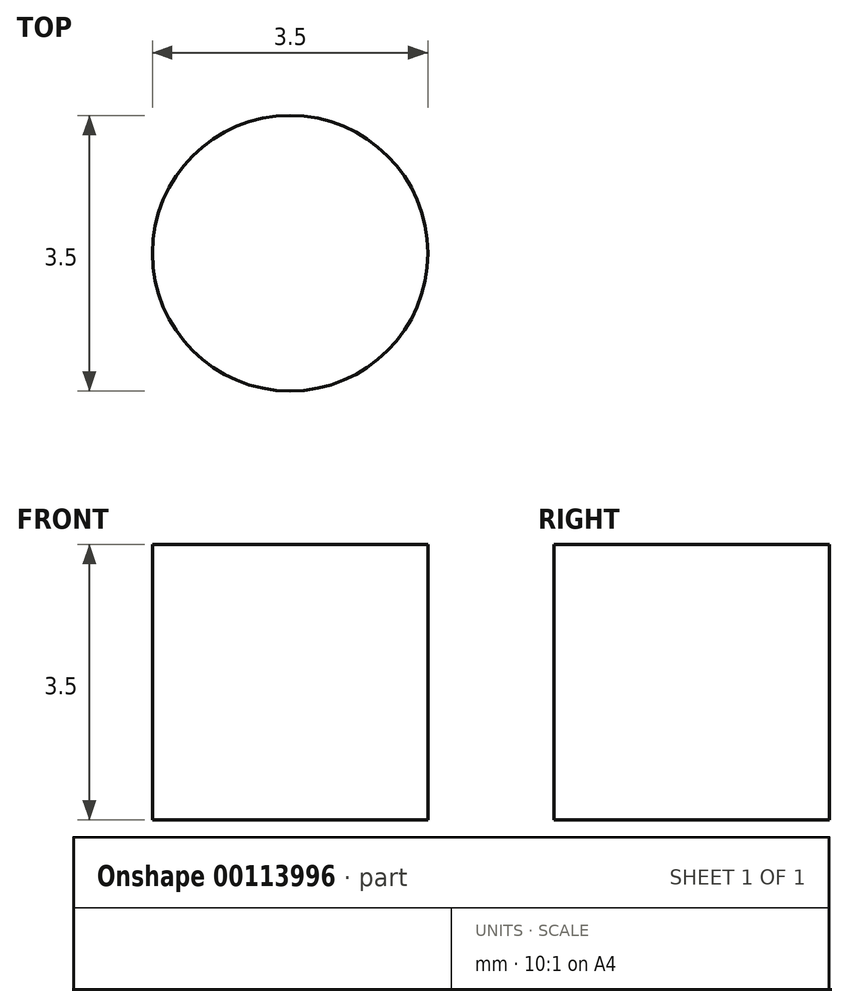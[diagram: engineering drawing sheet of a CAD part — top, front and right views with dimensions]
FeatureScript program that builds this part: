
annotation { "Feature Type Name" : "Feature", "Feature Type Description" : "" }
export const myFeature = defineFeature(function(context is Context, id is Id, definition is map)
    precondition{}
    {
        {
            var Q0;
            Q0=qCreatedBy(makeId("Right.planeOp"),FACE);
            var sketch = newSketch(context, id + "F0", { "sketchPlane" : qUnion([Q0])});
            skLineSegment(sketch, "E0.bottom", {"start": v(10, -3.07) * mm, "end": v(-10, -3.07) * mm});
            skLineSegment(sketch, "E0.top", {"start": v(10, 2.93) * mm, "end": v(-10, 2.93) * mm});
            skLineSegment(sketch, "E0.left", {"start": v(10, -3.07) * mm, "end": v(10, 2.93) * mm});
            skLineSegment(sketch, "E0.right", {"start": v(-10, -3.07) * mm, "end": v(-10, 2.93) * mm});
            skPoint(sketch, "E0.middle", {"position": v(0, -0.07) * mm});
            skLineSegment(sketch, "E1.bottom", {"start": v(-10, 1.43) * mm, "end": v(0, 1.43) * mm});
            skLineSegment(sketch, "E1.top", {"start": v(-10, -1.57) * mm, "end": v(0, -1.57) * mm});
            skLineSegment(sketch, "E1.left", {"start": v(-10, 1.43) * mm, "end": v(-10, -1.57) * mm});
            skLineSegment(sketch, "E1.right", {"start": v(0, 1.43) * mm, "end": v(0, -1.57) * mm});
            skSolve(sketch);
        }
        {
            var Q0;
            {var subQ1=sQuery(id+"F0.wireOp",EDGE,"E0.bottom");Q0=makeQuery(id+"F0.imprint","IMPRINT",FACE,{"disambiguationData":[TD([[makeQuery(id+"F0.imprint","IMPRINT",EDGE,{"derivedFrom":subQ1}),-1.0]])]});}
            var Q1;
            Q1=makeQuery(id+"F0.imprint","IMPRINT",FACE,{"disambiguationData":[TD([[makeQuery(id+"F0.imprint","IMPRINT",EDGE,{"derivedFrom":sQuery(id+"F0.wireOp",EDGE,"E1.bottom")}),-1.0]])]});
            extrude(context, id + "F1", {"entities" : qUnion([Q0, Q1]), "depth" : 10 * mm});
        }
        {
            var Q0;
            Q0=makeQuery(id+"F1.opExtrude","SWEPT_FACE",FACE,{"disambiguationData":[OSD([sQuery(id+"F0.wireOp",EDGE,"E0.top")])]});
            var sketch = newSketch(context, id + "F2", { "sketchPlane" : qUnion([Q0])});
            skLineSegment(sketch, "E2", {"start": v(10, 10) * mm, "end": v(0, 0) * mm});
            skCircle(sketch, "E3", {"center": v(5, 5) * mm, "radius": 1.75 * mm});
            skCircle(sketch, "E4", {"center": v(5, -5) * mm, "radius": 2.15 * mm});
            skSolve(sketch);
        }
        {
            var Q0;
            Q0=makeQuery(id+"F2.imprint","IMPRINT",FACE,{"disambiguationData":[TD([[makeQuery(id+"F2.imprint","IMPRINT",EDGE,{"derivedFrom":sQuery(id+"F2.wireOp",EDGE,"E4")}),1.0]])]});
            var Q1;
            {var subQ0=sQuery(id+"F2.wireOp",EDGE,"E3");var subQ1=sQuery(id+"F2.wireOp",EDGE,"E2");var subQ2=makeQuery(id+"F2.imprint","INTERSECT",VERTEX,{"disambiguationData":[OD(0.0)],"derivedFrom":[subQ1,subQ0]});Q1=makeQuery(id+"F2.imprint","IMPRINT",FACE,{"disambiguationData":[TD([[makeQuery(id+"F2.imprint","IMPRINT",EDGE,{"disambiguationData":[TD([[subQ2,-1.0]])],"derivedFrom":subQ1}),1.0]])]});}
            var Q2;
            {var subQ0=sQuery(id+"F2.wireOp",EDGE,"E3");var subQ1=sQuery(id+"F2.wireOp",EDGE,"E2");var subQ2=makeQuery(id+"F2.imprint","INTERSECT",VERTEX,{"disambiguationData":[OD(0.0)],"derivedFrom":[subQ1,subQ0]});Q2=makeQuery(id+"F2.imprint","IMPRINT",FACE,{"disambiguationData":[TD([[makeQuery(id+"F2.imprint","IMPRINT",EDGE,{"disambiguationData":[TD([[subQ2,-1.0]])],"derivedFrom":subQ1}),-1.0]])]});}
            extrude(context, id + "F3", {"entities" : qUnion([Q0, Q1, Q2]), "operationType" : NewBodyOperationType.REMOVE, "endBound" : BoundingType.UP_TO_NEXT, "oppositeDirection" : true, "depth" : 25 * mm});
        }
        {
            var Q0;
            Q0=makeQuery(id+"F1.opExtrude","SWEPT_FACE",FACE,{"disambiguationData":[OSD([sQuery(id+"F0.wireOp",EDGE,"E0.bottom")])]});
            var sketch = newSketch(context, id + "F4", { "sketchPlane" : qUnion([Q0])});
            skCircle(sketch, "E5.cCircle", {"center": v(5, -5) * mm, "radius": 2.8 * mm, "construction": true});
            skLineSegment(sketch, "E5.0", {"start": v(3.38, -7.8) * mm, "end": v(1.77, -5) * mm});
            skLineSegment(sketch, "E5.1", {"start": v(1.77, -5) * mm, "end": v(3.38, -2.2) * mm});
            skLineSegment(sketch, "E5.2", {"start": v(3.38, -2.2) * mm, "end": v(6.62, -2.2) * mm});
            skLineSegment(sketch, "E5.3", {"start": v(6.62, -2.2) * mm, "end": v(8.23, -5) * mm});
            skLineSegment(sketch, "E5.4", {"start": v(8.23, -5) * mm, "end": v(6.62, -7.8) * mm});
            skLineSegment(sketch, "E5.5", {"start": v(6.62, -7.8) * mm, "end": v(3.38, -7.8) * mm});
            skPoint(sketch, "E5.0.midPoint", {"position": v(2.58, -6.4) * mm});
            skSolve(sketch);
        }
        {
            var Q0;
            Q0 = qSketchRegion(id + "F4", true);
            extrude(context, id + "F5", {"entities" : qUnion([Q0]), "operationType" : NewBodyOperationType.REMOVE, "oppositeDirection" : true, "depth" : 2.5 * mm});
        }
        {
            var Q0;
            Q0=makeQuery(id+"F1.opExtrude","SWEPT_FACE",FACE,{"disambiguationData":[OSD([sQuery(id+"F0.wireOp",EDGE,"E0.top")])]});
            var sketch = newSketch(context, id + "F6", { "sketchPlane" : qUnion([Q0])});
            skCircle(sketch, "E6", {"center": v(5, -5) * mm, "radius": 3.65 * mm});
            skSolve(sketch);
        }
        {
            var Q0;
            Q0 = qSketchRegion(id + "F6", true);
            extrude(context, id + "F7", {"entities" : qUnion([Q0]), "operationType" : NewBodyOperationType.REMOVE, "oppositeDirection" : true, "depth" : 3 * mm});
        }
        {
            var Q0;
            Q0=makeQuery(id+"F1.opExtrude","SWEPT_FACE",FACE,{"disambiguationData":[OSD([sQuery(id+"F0.wireOp",EDGE,"E0.top")])]});
            var sketch = newSketch(context, id + "F8", { "sketchPlane" : qUnion([Q0])});
            skLineSegment(sketch, "E7.bottom", {"start": v(0, -10) * mm, "end": v(10, -10) * mm});
            skArc(sketch, "E8", {"start": v(10, -5.68) * mm, "mid": v(5, -1.39) * mm, "end": v(0, -5.68) * mm});
            skLineSegment(sketch, "E9", {"start": v(0, -5.68) * mm, "end": v(0, -10) * mm});
            skLineSegment(sketch, "E10", {"start": v(10, -5.68) * mm, "end": v(10, -10) * mm});
            skSolve(sketch);
        }
        {
            var Q0;
            Q0 = qSketchRegion(id + "F8", true);
            extrude(context, id + "F9", {"entities" : qUnion([Q0]), "operationType" : NewBodyOperationType.REMOVE, "oppositeDirection" : true, "depth" : 3 * mm});
        }
    });
